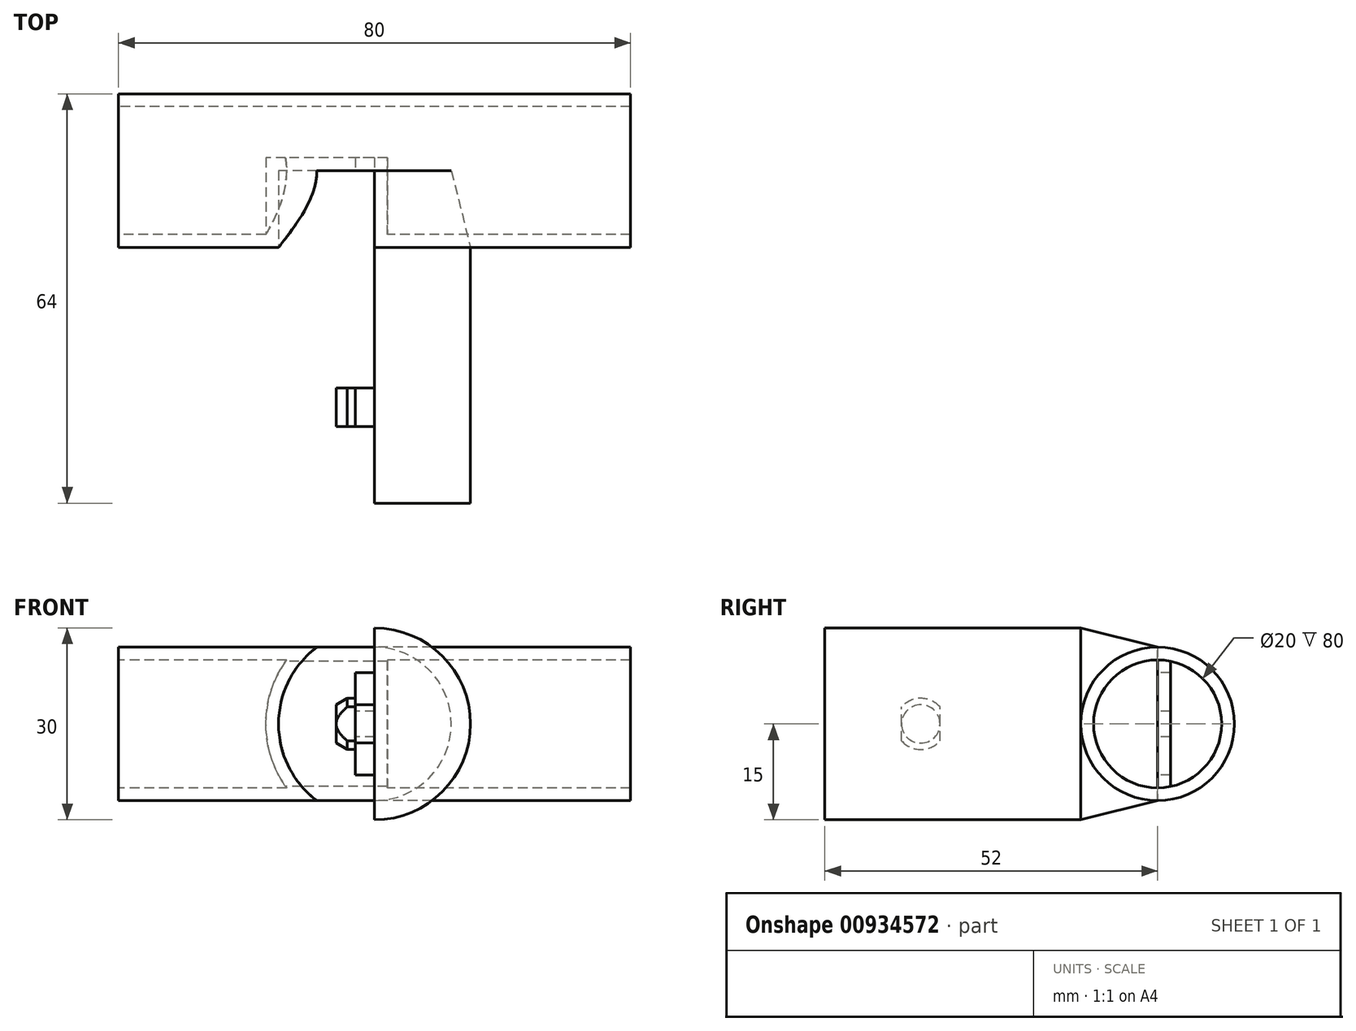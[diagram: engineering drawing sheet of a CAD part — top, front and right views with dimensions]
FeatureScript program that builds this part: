
annotation { "Feature Type Name" : "Feature", "Feature Type Description" : "" }
export const myFeature = defineFeature(function(context is Context, id is Id, definition is map)
    precondition{}
    {
        {
            var Q0;
            Q0=qCreatedBy(makeId("Right.planeOp"),FACE);
            var sketch = newSketch(context, id + "F0", { "sketchPlane" : qUnion([Q0])});
            skCircle(sketch, "E0", {"center": v(0, 0) * mm, "radius": 12 * mm});
            skSolve(sketch);
        }
        {
            var Q0;
            Q0 = qSketchRegion(id + "F0", true);
            extrude(context, id + "F1", {"entities" : qUnion([Q0]), "depth" : 40 * mm, "offsetDistance" : 25 * mm});
        }
        {
            var Q0;
            Q0=makeQuery(id+"F1.opExtrude","CAP_FACE",FACE,{"disambiguationData":[OSD([sQuery(id+"F0.wireOp",EDGE,"pNDSs2QC-sM8T-hz3y-3pqi-EhfsqSjqK6pL"),sQuery(id+"F0.wireOp",EDGE,"E0")])],"isStart":true});
            extrude(context, id + "F2", {"entities" : qUnion([Q0]), "operationType" : NewBodyOperationType.ADD, "depth" : 40 * mm, "offsetDistance" : 25 * mm});
        }
        {
            var Q0;
            Q0=qCreatedBy(makeId("Front.planeOp"),FACE);
            var sketch = newSketch(context, id + "F3", { "sketchPlane" : qUnion([Q0])});
            skCircle(sketch, "E1", {"center": v(0, 0) * mm, "radius": 12 * mm});
            skSolve(sketch);
        }
        {
            var Q0;
            Q0=qCreatedBy(makeId("Front.planeOp"),FACE);
            cPlane(context, id + "F4", {"entities" : qUnion([Q0]), "cplaneType" : CPlaneType.OFFSET, "offset" : 12 * mm, "width" : 150 * mm, "height" : 150 * mm});
        }
        {
            var Q0;
            Q0=qCreatedBy(id+"F4.planeOp",FACE);
            var sketch = newSketch(context, id + "F5", { "sketchPlane" : qUnion([Q0])});
            skCircle(sketch, "E2", {"center": v(0, 0) * mm, "radius": 15 * mm});
            skSolve(sketch);
        }
        {
            var Q0;
            Q0=makeQuery(id+"F5.imprint","IMPRINT",FACE,{"disambiguationData":[TD([[makeQuery(id+"F5.imprint","IMPRINT",EDGE,{"derivedFrom":sQuery(id+"F5.wireOp",EDGE,"E2")}),1.0]])]});
            extrude(context, id + "F6", {"entities" : qUnion([Q0]), "operationType" : NewBodyOperationType.ADD, "depth" : 40 * mm, "offsetDistance" : 25 * mm});
        }
        {
            var Q0;
            Q0=makeQuery(id+"F3.imprint","IMPRINT",FACE,{"disambiguationData":[TD([[makeQuery(id+"F3.imprint","IMPRINT",EDGE,{"derivedFrom":sQuery(id+"F3.wireOp",EDGE,"E1")}),1.0]])]});
            var Q1;
            Q1=makeQuery(id+"F6.opExtrude","CAP_FACE",FACE,{"disambiguationData":[OSD([sQuery(id+"F5.wireOp",EDGE,"E2")])],"isStart":true});
            loft(context, id + "F7", {"sheetProfilesArray" : [{ "sheetProfileEntities" : qUnion([Q0]) }, { "sheetProfileEntities" : qUnion([Q1]) }]});
        }
        {
            var Q0;
            Q0=makeQuery(id+"F6.opExtrude","CAP_FACE",FACE,{"disambiguationData":[OSD([sQuery(id+"F5.wireOp",EDGE,"E2")])],"isStart":false});
            var sketch = newSketch(context, id + "F8", { "sketchPlane" : qUnion([Q0])});
            skLineSegment(sketch, "E3", {"start": v(0, 0) * mm, "end": v(0, 15) * mm});
            skLineSegment(sketch, "E4", {"start": v(0, 15) * mm, "end": v(0, -15) * mm});
            skSolve(sketch);
        }
        {
            var Q0;
            {var subQ0=sQuery(id+"F8.wireOp",EDGE,"E4");var subQ3=makeQuery(id+"F8.imprint","IMPRINT",VERTEX,{"derivedFrom":subQ0});Q0=makeQuery(id+"F8.imprint","IMPRINT",FACE,{"disambiguationData":[TD([[makeQuery(id+"F8.imprint","IMPRINT",EDGE,{"disambiguationData":[TD([[subQ3,1.0]])],"derivedFrom":subQ0}),-1.0]])]});}
            extrude(context, id + "F9", {"entities" : qUnion([Q0]), "operationType" : NewBodyOperationType.REMOVE, "oppositeDirection" : true, "depth" : 52 * mm, "offsetDistance" : 25 * mm});
        }
        {
            var Q0;
            Q0=qCreatedBy(makeId("Top.planeOp"),FACE);
            var sketch = newSketch(context, id + "F10", { "sketchPlane" : qUnion([Q0])});
            skLineSegment(sketch, "E5", {"start": v(0, 0) * mm, "end": v(0, -12) * mm});
            skLineSegment(sketch, "E6", {"start": v(0, -12) * mm, "end": v(-15, -12) * mm});
            skLineSegment(sketch, "E7", {"start": v(-15, -12) * mm, "end": v(0, 0) * mm});
            skSolve(sketch);
        }
        {
            var Q0;
            Q0 = qSketchRegion(id + "F10", true);
            extrude(context, id + "F11", {"entities" : qUnion([Q0]), "operationType" : NewBodyOperationType.REMOVE, "oppositeDirection" : true, "depth" : 25 * mm, "offsetDistance" : 25 * mm});
        }
        {
            var Q0;
            Q0 = qSketchRegion(id + "F10", true);
            extrude(context, id + "F12", {"entities" : qUnion([Q0]), "operationType" : NewBodyOperationType.REMOVE, "depth" : 25 * mm, "offsetDistance" : 25 * mm});
        }
        {
            var Q0;
            Q0=makeQuery(id+"F1.opExtrude","CAP_FACE",FACE,{"disambiguationData":[OSD([sQuery(id+"F0.wireOp",EDGE,"E0")])],"isStart":false});
            var Q1;
            Q1=makeQuery(id+"F2.opExtrude","CAP_FACE",FACE,{"disambiguationData":[OSD([sQuery(id+"F0.wireOp",EDGE,"E0")])],"isStart":false});
            shell(context, id + "F13", {"entities" : qUnion([Q0, Q1]), "thickness" : 2 * mm});
        }
        {
            var Q0;
            Q0=makeQuery(id+"F1.opExtrude","SWEPT_BODY",BODY,{"disambiguationData":[OSD([sQuery(id+"F0.wireOp",EDGE,"E0")])]});
            var Q1;
            Q1=makeQuery(id+"F6.opExtrude","SWEPT_BODY",BODY,{"disambiguationData":[OSD([sQuery(id+"F5.wireOp",EDGE,"E2")])]});
            booleanBodies(context, id + "F14", {"operationType" : BooleanOperationType.UNION, "tools" : qUnion([Q0, Q1])});
        }
        {
            var Q0;
            {var subQ0=sQuery(id+"F10.wireOp",EDGE,"E5");Q0=makeQuery(id+"F14.opBoolean","MERGE",FACE,{"derivedFrom":[makeQuery(id+"F12.boolean.opBoolean","MERGE",FACE,{"derivedFrom":[makeQuery(id+"F11.boolean.opBoolean","COPY",FACE,{"derivedFrom":makeQuery(id+"F11.opExtrude","SWEPT_FACE",FACE,{"disambiguationData":[OSD([subQ0])]})})],"fromTools":[makeQuery(id+"F12.opExtrude","SWEPT_FACE",FACE,{"disambiguationData":[OSD([subQ0])]})]}),makeQuery(id+"F9.boolean.opBoolean","COPY",FACE,{"derivedFrom":makeQuery(id+"F9.opExtrude","SWEPT_FACE",FACE,{"disambiguationData":[OSD([sQuery(id+"F8.wireOp",EDGE,"E4")])]})})]});}
            var sketch = newSketch(context, id + "F15", { "sketchPlane" : qUnion([Q0])});
            skCircle(sketch, "E8", {"center": v(37, 0) * mm, "radius": 3 * mm});
            skPoint(sketch, "E8.centerSnap0", {"position": v(52, 0) * mm});
            skSolve(sketch);
        }
        {
            var Q0;
            Q0=makeQuery(id+"F15.imprint","IMPRINT",FACE,{"disambiguationData":[TD([[makeQuery(id+"F15.imprint","IMPRINT",EDGE,{"derivedFrom":sQuery(id+"F15.wireOp",EDGE,"E8")}),1.0]])]});
            extrude(context, id + "F16", {"entities" : qUnion([Q0]), "operationType" : NewBodyOperationType.ADD, "depth" : 3 * mm, "offsetDistance" : 25 * mm});
        }
        {
            var Q0;
            Q0=makeQuery(id+"F16.opExtrude","CAP_FACE",FACE,{"disambiguationData":[OSD([sQuery(id+"F15.wireOp",EDGE,"E8")])],"isStart":false});
            var sketch = newSketch(context, id + "F17", { "sketchPlane" : qUnion([Q0])});
            skCircle(sketch, "E9", {"center": v(37, 0) * mm, "radius": 4 * mm});
            skSolve(sketch);
        }
        {
            var Q0;
            Q0=makeQuery(id+"F17.imprint","IMPRINT",FACE,{"disambiguationData":[TD([[makeQuery(id+"F17.imprint","IMPRINT",EDGE,{"derivedFrom":sQuery(id+"F17.wireOp",EDGE,"E9")}),1.0]])]});
            var Q1;
            Q1=makeQuery(id+"F17.imprint","IMPRINT",FACE,{"disambiguationData":[TD([[makeQuery(id+"F17.imprint","IMPRINT",EDGE,{"derivedFrom":makeQuery(id+"F16.opExtrude","CAP_EDGE",EDGE,{"disambiguationData":[OSD([sQuery(id+"F15.wireOp",EDGE,"E8")])],"isStart":false})}),1.0]])]});
            extrude(context, id + "F18", {"entities" : qUnion([Q0, Q1]), "operationType" : NewBodyOperationType.ADD, "depth" : 3 * mm, "offsetDistance" : 25 * mm});
        }
        {
            var Q0;
            Q0=makeQuery(id+"F18.opExtrude","CAP_EDGE",EDGE,{"disambiguationData":[OSD([sQuery(id+"F17.wireOp",EDGE,"E9")])],"isStart":false});
            chamfer(context, id + "F19", {"entities" : qUnion([Q0]), "chamferType" : ChamferType.OFFSET_ANGLE, "width" : 1 * mm, "oppositeDirection" : false, "angle" : 60 * degree, "tangentPropagation" : true});
        }
        {
            var Q0;
            {var subQ0=sQuery(id+"F10.wireOp",EDGE,"E5");Q0=makeQuery(id+"F14.opBoolean","MERGE",FACE,{"derivedFrom":[makeQuery(id+"F12.boolean.opBoolean","MERGE",FACE,{"derivedFrom":[makeQuery(id+"F11.boolean.opBoolean","COPY",FACE,{"derivedFrom":makeQuery(id+"F11.opExtrude","SWEPT_FACE",FACE,{"disambiguationData":[OSD([subQ0])]})})],"fromTools":[makeQuery(id+"F12.opExtrude","SWEPT_FACE",FACE,{"disambiguationData":[OSD([subQ0])]})]}),makeQuery(id+"F9.boolean.opBoolean","COPY",FACE,{"derivedFrom":makeQuery(id+"F9.opExtrude","SWEPT_FACE",FACE,{"disambiguationData":[OSD([sQuery(id+"F8.wireOp",EDGE,"E4")])]})})]});}
            var sketch = newSketch(context, id + "F20", { "sketchPlane" : qUnion([Q0])});
            skLineSegment(sketch, "E10", {"start": v(34, 0) * mm, "end": v(34, -6.3) * mm});
            skLineSegment(sketch, "E11", {"start": v(34, -6.3) * mm, "end": v(30.28, -6.3) * mm});
            skLineSegment(sketch, "E12", {"start": v(30.28, -6.3) * mm, "end": v(30.28, 6.05) * mm});
            skLineSegment(sketch, "E13", {"start": v(30.28, 6.05) * mm, "end": v(34, 6.05) * mm});
            skLineSegment(sketch, "E14", {"start": v(34, 6.05) * mm, "end": v(34, 0) * mm});
            skLineSegment(sketch, "E15", {"start": v(40, 0) * mm, "end": v(40, -6.55) * mm});
            skLineSegment(sketch, "E16", {"start": v(40, -6.55) * mm, "end": v(44.46, -6.55) * mm});
            skLineSegment(sketch, "E17", {"start": v(44.46, -6.55) * mm, "end": v(44.46, 6.05) * mm});
            skLineSegment(sketch, "E18", {"start": v(44.46, 6.05) * mm, "end": v(40, 6.05) * mm});
            skLineSegment(sketch, "E19", {"start": v(40, 6.05) * mm, "end": v(40, 0) * mm});
            skSolve(sketch);
        }
        {
            var Q0;
            Q0=makeQuery(id+"F7.opLoft","CAP_FACE",FACE,{"disambiguationData":[OSD([makeQuery(id+"F3.imprint","IMPRINT",FACE,{"disambiguationData":[TD([[makeQuery(id+"F3.imprint","IMPRINT",EDGE,{"derivedFrom":sQuery(id+"F3.wireOp",EDGE,"E1")}),1.0]])]})])],"isStart":true});
            var sketch = newSketch(context, id + "F21", { "sketchPlane" : qUnion([Q0])});
            skLineSegment(sketch, "E20.bottom", {"start": v(0, 2) * mm, "end": v(3, 2) * mm});
            skLineSegment(sketch, "E20.top", {"start": v(0, 8) * mm, "end": v(3, 8) * mm});
            skLineSegment(sketch, "E20.left", {"start": v(0, 2) * mm, "end": v(0, 8) * mm});
            skLineSegment(sketch, "E20.right", {"start": v(3, 2) * mm, "end": v(3, 8) * mm});
            skLineSegment(sketch, "E21.bottom", {"start": v(0, -2) * mm, "end": v(3, -2) * mm});
            skLineSegment(sketch, "E21.top", {"start": v(0, -8) * mm, "end": v(3, -8) * mm});
            skLineSegment(sketch, "E21.left", {"start": v(0, -2) * mm, "end": v(0, -8) * mm});
            skLineSegment(sketch, "E21.right", {"start": v(3, -2) * mm, "end": v(3, -8) * mm});
            skSolve(sketch);
        }
        {
            var Q0;
            Q0 = qSketchRegion(id + "F21", true);
            extrude(context, id + "F22", {"entities" : qUnion([Q0]), "operationType" : NewBodyOperationType.REMOVE, "oppositeDirection" : true, "depth" : 25 * mm, "offsetDistance" : 25 * mm});
        }
        {
            var Q0;
            Q0 = qSketchRegion(id + "F21", true);
            extrude(context, id + "F23", {"entities" : qUnion([Q0]), "operationType" : NewBodyOperationType.REMOVE, "depth" : 4.9 * mm, "offsetDistance" : 25 * mm});
        }
        {
            var Q0;
            Q0=makeQuery(id+"F20.imprint","IMPRINT",FACE,{"disambiguationData":[TD([[makeQuery(id+"F20.imprint","IMPRINT",EDGE,{"derivedFrom":sQuery(id+"F20.wireOp",EDGE,"E10")}),-1.0]])]});
            var Q1;
            Q1=makeQuery(id+"F20.imprint","IMPRINT",FACE,{"disambiguationData":[TD([[makeQuery(id+"F20.imprint","IMPRINT",EDGE,{"derivedFrom":sQuery(id+"F20.wireOp",EDGE,"E15")}),1.0]])]});
            extrude(context, id + "F24", {"entities" : qUnion([Q0, Q1]), "operationType" : NewBodyOperationType.REMOVE, "depth" : 25 * mm, "offsetDistance" : 25 * mm});
        }
    });
